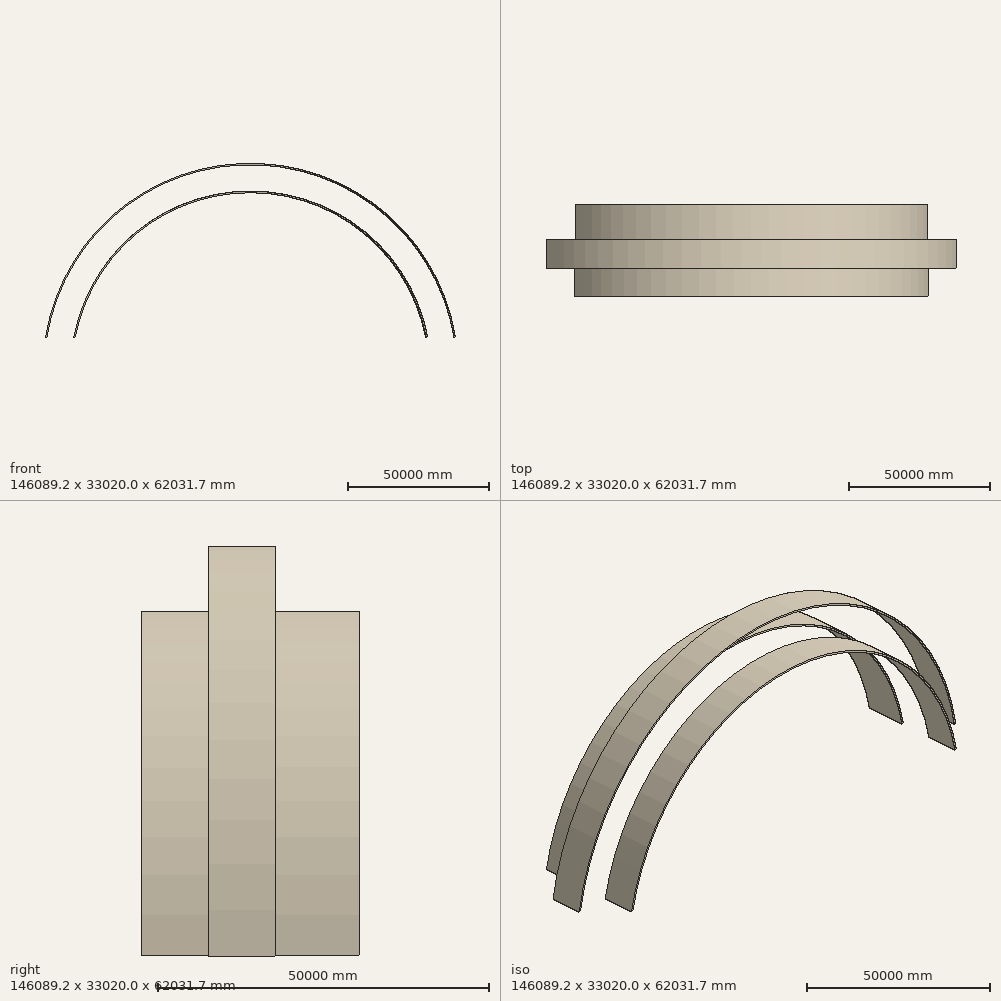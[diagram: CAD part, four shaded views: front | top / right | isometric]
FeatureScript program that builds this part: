
annotation { "Feature Type Name" : "Feature", "Feature Type Description" : "" }
export const myFeature = defineFeature(function(context is Context, id is Id, definition is map)
    precondition{}
    {
        {
            var Q0;
            Q0=qCreatedBy(makeId("Front.planeOp"),FACE);
            var sketch = newSketch(context, id + "F0", { "sketchPlane" : qUnion([Q0])});
            skArc(sketch, "E0", {"start": v(124771.04, 0) * mm, "mid": v(62385.52, 51655.3) * mm, "end": v(0, 0) * mm});
            skArc(sketch, "E1.0", {"start": v(125270.12, 94.76) * mm, "mid": v(62385.52, 52163.3) * mm, "end": v(-499.09, 94.76) * mm});
            skLineSegment(sketch, "E2", {"start": v(-499.09, 94.76) * mm, "end": v(18.07, 94.76) * mm});
            skLineSegment(sketch, "E3.trimOffspring", {"start": v(124752.97, 94.76) * mm, "end": v(125270.12, 94.76) * mm});
            skSolve(sketch);
        }
        {
            var Q0;
            Q0 = qSketchRegion(id + "F0", true);
            extrude(context, id + "F1", {"entities" : qUnion([Q0]), "depth" : 12700 * mm, "offsetDistance" : 25.4 * mm});
        }
        {
            var Q0;
            Q0=makeQuery(id+"F1.opExtrude","CAP_FACE",FACE,{"disambiguationData":[OSD([sQuery(id+"F0.wireOp",EDGE,"E0"),sQuery(id+"F0.wireOp",EDGE,"E1.0"),sQuery(id+"F0.wireOp",EDGE,"E2"),sQuery(id+"F0.wireOp",EDGE,"E3.trimOffspring")])],"isStart":false});
            var sketch = newSketch(context, id + "F2", { "sketchPlane" : qUnion([Q0])});
            skArc(sketch, "E4", {"start": v(135430.12, 0) * mm, "mid": v(62385.52, 62031.7) * mm, "end": v(-10659.09, 0) * mm});
            skArc(sketch, "E5.0", {"start": v(134915.28, 0) * mm, "mid": v(62385.52, 61523.7) * mm, "end": v(-10144.24, 0) * mm});
            skLineSegment(sketch, "E6", {"start": v(-10659.09, 0) * mm, "end": v(-10144.24, 0) * mm});
            skPoint(sketch, "E7.end.orphan", {"position": v(134928.83, 0) * mm});
            skLineSegment(sketch, "E8", {"start": v(135430.12, 0) * mm, "end": v(134915.28, 0) * mm});
            skPoint(sketch, "E9.orphan", {"position": v(134928.83, -82.29) * mm});
            skSolve(sketch);
        }
        {
            var Q0;
            Q0 = qSketchRegion(id + "F2", true);
            extrude(context, id + "F3", {"entities" : qUnion([Q0]), "depth" : 10160 * mm, "offsetDistance" : 25.4 * mm});
        }
        {
            var Q0;
            Q0=makeQuery(id+"F3.opExtrude","CAP_FACE",FACE,{"disambiguationData":[OSD([sQuery(id+"F2.wireOp",EDGE,"E4"),sQuery(id+"F2.wireOp",EDGE,"E5.0"),sQuery(id+"F2.wireOp",EDGE,"E6"),sQuery(id+"F2.wireOp",EDGE,"E8")])],"isStart":false});
            var sketch = newSketch(context, id + "F4", { "sketchPlane" : qUnion([Q0])});
            skArc(sketch, "E10", {"start": v(124975.6, 106.25) * mm, "mid": v(62498.13, 51555.2) * mm, "end": v(20.67, 106.25) * mm});
            skArc(sketch, "E11.0", {"start": v(125544.87, 106.25) * mm, "mid": v(62498.13, 52114) * mm, "end": v(-548.6, 106.25) * mm});
            skLineSegment(sketch, "E12", {"start": v(-548.6, 106.25) * mm, "end": v(20.67, 106.25) * mm});
            skLineSegment(sketch, "E13", {"start": v(125544.87, 106.25) * mm, "end": v(124975.6, 106.25) * mm});
            skPoint(sketch, "E14.orphan", {"position": v(124996.27, 0) * mm});
            skSolve(sketch);
        }
        {
            var Q0;
            Q0 = qSketchRegion(id + "F4", true);
            extrude(context, id + "F5", {"entities" : qUnion([Q0]), "depth" : 10160 * mm, "offsetDistance" : 25.4 * mm});
        }
        {
            var Q0;
            Q0=makeQuery(id+"F3.opExtrude","CAP_FACE",FACE,{"disambiguationData":[OSD([sQuery(id+"F2.wireOp",EDGE,"E4"),sQuery(id+"F2.wireOp",EDGE,"E5.0"),sQuery(id+"F2.wireOp",EDGE,"E6"),sQuery(id+"F2.wireOp",EDGE,"E8")])],"isStart":false});
            var sketch = newSketch(context, id + "F6", { "sketchPlane" : qUnion([Q0])});
            skCircle(sketch, "E15", {"center": v(8495.23, 30513.28) * mm, "radius": 4749.46 * mm});
            skCircle(sketch, "E16.1.0", {"center": v(21723.05, 43302.35) * mm, "radius": 4749.46 * mm});
            skCircle(sketch, "E16.2.0", {"center": v(37873.08, 52117.8) * mm, "radius": 4749.46 * mm});
            skCircle(sketch, "E16.3.0", {"center": v(55784.68, 56326.14) * mm, "radius": 4749.46 * mm});
            skCircle(sketch, "E16.4.0", {"center": v(74170.65, 55624.93) * mm, "radius": 4749.46 * mm});
            skCircle(sketch, "E16.5.0", {"center": v(91709.68, 50064.54) * mm, "radius": 4749.46 * mm});
            skCircle(sketch, "E16.6.0", {"center": v(107141.35, 40044.6) * mm, "radius": 4749.46 * mm});
            skCircle(sketch, "E16.7.0", {"center": v(119356.64, 26285.16) * mm, "radius": 4749.46 * mm});
            skPoint(sketch, "E16.center", {"position": v(62385.52, -11990.5) * mm});
            skLineSegment(sketch, "E16.anchor1", {"start": v(62385.52, -11990.5) * mm, "end": v(8495.23, 30513.28) * mm, "construction": true});
            skLineSegment(sketch, "E16.anchor2", {"start": v(62385.52, -11990.5) * mm, "end": v(119356.64, 26285.16) * mm, "construction": true});
            skSolve(sketch);
        }
        {
            var Q0;
            Q0=sQuery(id+"F6.wireOp",EDGE,"E15");
            var Q1;
            Q1=sQuery(id+"F6.wireOp",EDGE,"E16.1.0");
            var Q2;
            Q2=sQuery(id+"F6.wireOp",EDGE,"E16.2.0");
            var Q3;
            Q3=sQuery(id+"F6.wireOp",EDGE,"E16.3.0");
            var Q4;
            Q4=sQuery(id+"F6.wireOp",EDGE,"E16.4.0");
            var Q5;
            Q5=sQuery(id+"F6.wireOp",EDGE,"E16.5.0");
            var Q6;
            Q6=sQuery(id+"F6.wireOp",EDGE,"E16.6.0");
            var Q7;
            Q7=sQuery(id+"F6.wireOp",EDGE,"E16.7.0");
            extrude(context, id + "F7", {"bodyType" : ToolBodyType.SURFACE, "surfaceEntities" : qUnion([Q0, Q1, Q2, Q3, Q4, Q5, Q6, Q7]), "oppositeDirection" : true, "depth" : 10160 * mm, "offsetDistance" : 25.4 * mm});
        }
    });
